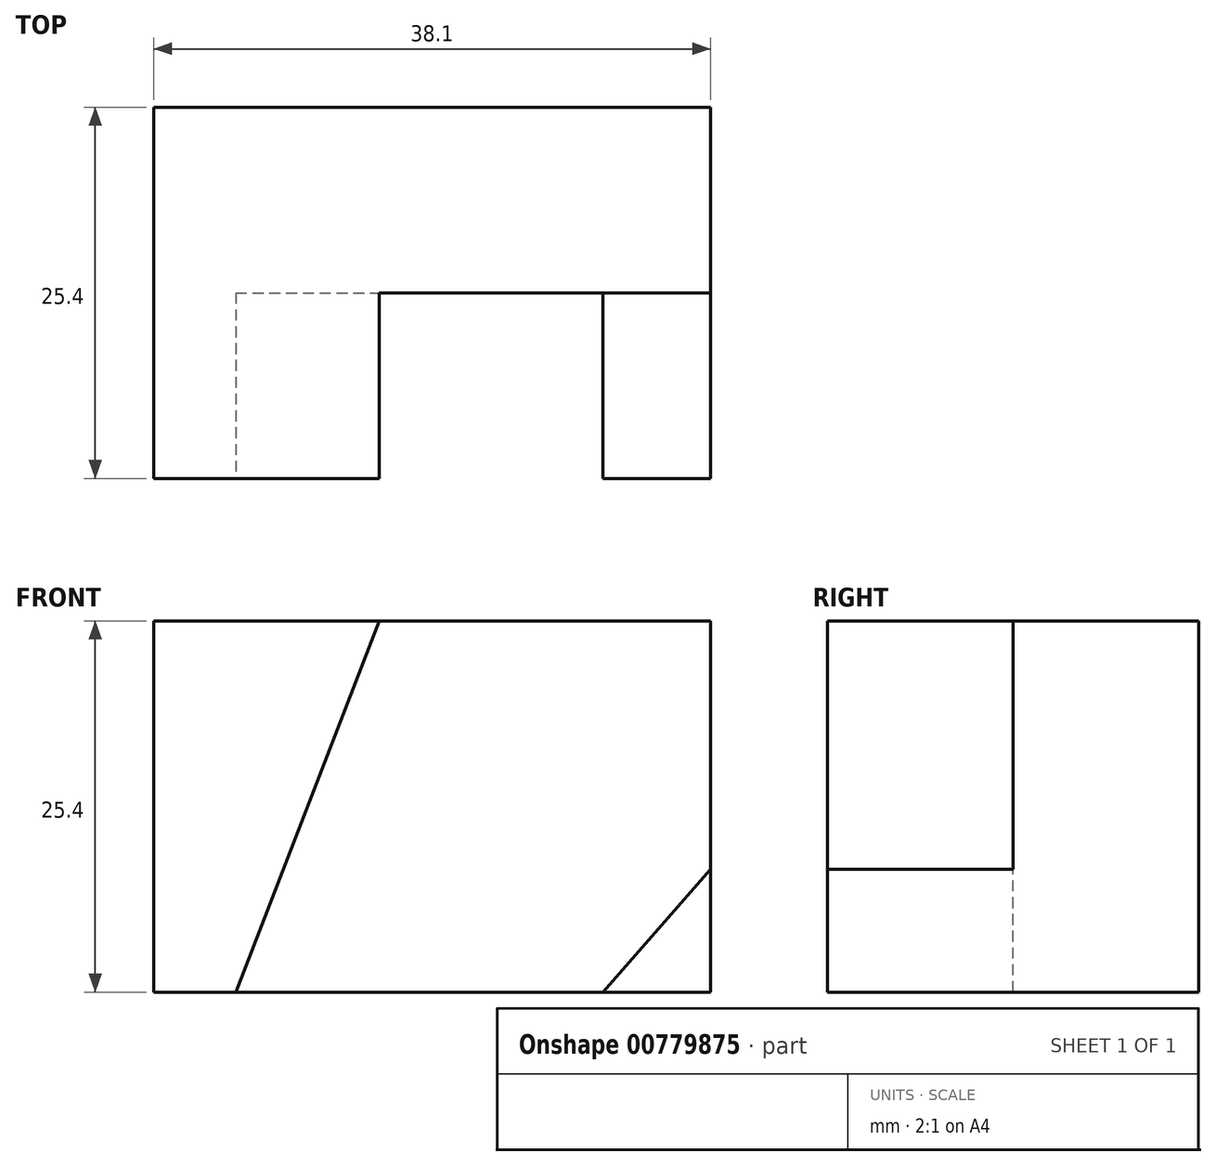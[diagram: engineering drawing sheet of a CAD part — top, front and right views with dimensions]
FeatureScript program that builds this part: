
annotation { "Feature Type Name" : "Feature", "Feature Type Description" : "" }
export const myFeature = defineFeature(function(context is Context, id is Id, definition is map)
    precondition{}
    {
        {
            var Q0;
            Q0=qCreatedBy(makeId("Front.planeOp"),FACE);
            var sketch = newSketch(context, id + "F0", { "sketchPlane" : qUnion([Q0])});
            skLineSegment(sketch, "E0", {"start": v(0, 25.4) * mm, "end": v(0, 0) * mm});
            skLineSegment(sketch, "E1", {"start": v(0, 0) * mm, "end": v(38.1, 0) * mm});
            skLineSegment(sketch, "E2", {"start": v(38.1, 0) * mm, "end": v(38.1, 25.4) * mm});
            skLineSegment(sketch, "E3", {"start": v(0, 25.4) * mm, "end": v(38.1, 25.4) * mm});
            skSolve(sketch);
        }
        {
            var Q0;
            Q0 = qSketchRegion(id + "F0", true);
            extrude(context, id + "F1", {"entities" : qUnion([Q0]), "depth" : 25.4 * mm, "offsetDistance" : 25.4 * mm});
        }
        {
            var Q0;
            Q0=makeQuery(id+"F1.opExtrude","CAP_FACE",FACE,{"disambiguationData":[OSD([sQuery(id+"F0.wireOp",EDGE,"E0"),sQuery(id+"F0.wireOp",EDGE,"E1"),sQuery(id+"F0.wireOp",EDGE,"E2"),sQuery(id+"F0.wireOp",EDGE,"E3")])],"isStart":false});
            var sketch = newSketch(context, id + "F2", { "sketchPlane" : qUnion([Q0])});
            skLineSegment(sketch, "E4", {"start": v(5.6, 0) * mm, "end": v(15.43, 25.4) * mm});
            skLineSegment(sketch, "E5", {"start": v(15.43, 25.4) * mm, "end": v(38.1, 25.4) * mm});
            skLineSegment(sketch, "E6", {"start": v(38.1, 25.4) * mm, "end": v(38.1, 0) * mm});
            skLineSegment(sketch, "E7", {"start": v(38.1, 0) * mm, "end": v(30.73, 0) * mm});
            skLineSegment(sketch, "E8", {"start": v(30.73, 0) * mm, "end": v(38.1, 8.4) * mm});
            skSolve(sketch);
        }
        {
            var Q0;
            {var subQ3=sQuery(id+"F2.wireOp",EDGE,"E4");Q0=makeQuery(id+"F2.imprint","IMPRINT",FACE,{"disambiguationData":[TD([[makeQuery(id+"F2.imprint","IMPRINT",EDGE,{"derivedFrom":subQ3}),-1.0]])]});}
            extrude(context, id + "F3", {"entities" : qUnion([Q0]), "operationType" : NewBodyOperationType.REMOVE, "oppositeDirection" : true, "depth" : 12.7 * mm, "offsetDistance" : 25.4 * mm});
        }
    });
